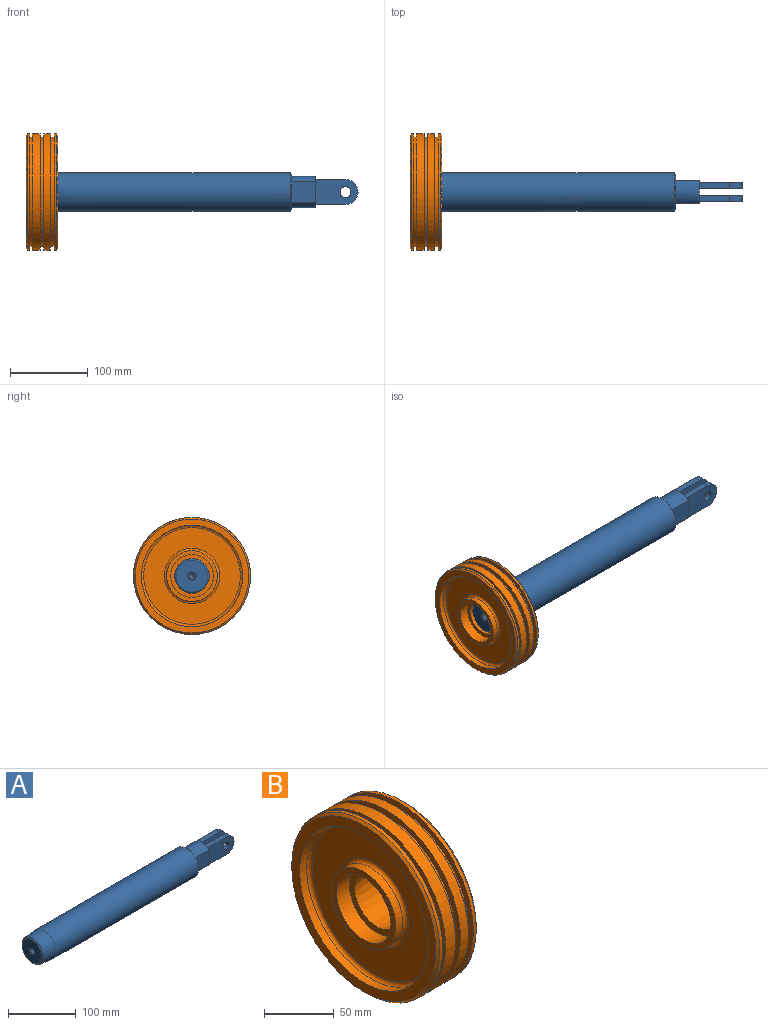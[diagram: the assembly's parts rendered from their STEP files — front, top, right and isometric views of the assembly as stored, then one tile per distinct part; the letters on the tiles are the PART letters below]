
ASSEMBLY  parts=2 mates=1
PART A: 28 faces, bbox 410x50x50 mm
  f0: plane 32x3mm, normal (1,0,0), area 88.3mm2, adj f1,f4,f21,f24
  f1: cylinder r=20mm len=30mm, axis (1,0,0), area 1017.7mm2, adj f0,f2,f3,f5,f23,f24
  f2: plane 40x24mm, normal (1,0,0), area 386.8mm2, adj f1,f4,f11,f12,f16,f17,f19,f22
  f3: plane 32x3mm, normal (1,0,0), area 88.3mm2, adj f1,f4,f15,f23
  f4: cylinder r=20mm len=30mm, axis (1,0,0), area 1017.7mm2, adj f0,f2,f3,f5,f23,f24
  f5: plane 45.58x45.58mm, normal (1,0,0), area 556.4mm2, adj f1,f4,f9,f23,f24
  f6: cylinder r=25mm len=297.79mm, axis (1,0,0), area 46776.8mm2, adj f7,f9
  f7: cone r=22.5mm half-angle=5.7deg, axis (1,0,0), area 3465.5mm2, adj f6,f10
  f8: plane 41.01x41.01mm, normal (-1,0,0), area 1234.3mm2, adj f10,f27
  f9: cone r=22.79mm half-angle=45deg, axis (-1,0,0), area 469.2mm2, adj f5,f6
  f10: cone r=22.7mm half-angle=47.8deg, axis (1,0,0), area 402.6mm2, adj f7,f8
  f11: plane 39x8mm, normal (0,0,1), area 312mm2, adj f2,f14,f15,f16
  f12: plane 39x8mm, normal (0,0,-1), area 312mm2, adj f2,f14,f15,f16
  f13: cylinder r=7mm len=14mm, axis (0,1,0), area 351.9mm2, adj f15,f16
  f14: cylinder r=16mm len=32mm, axis (0,1,0), area 402.1mm2, adj f11,f12,f15,f16
  f15: plane 55x32mm, normal (0,-1,0), area 1496.2mm2, adj f3,f11,f12,f13,f14
  f16: plane 55x32mm, normal (0,1,0), area 1496.2mm2, adj f2,f11,f12,f13,f14
  f17: plane 39x8mm, normal (0,0,1), area 312mm2, adj f2,f18,f21,f22
  f18: cylinder r=16mm len=32mm, axis (0,-1,0), area 402.1mm2, adj f17,f19,f21,f22
  f19: plane 39x8mm, normal (0,0,-1), area 312mm2, adj f2,f18,f21,f22
  f20: cylinder r=7mm len=14mm, axis (0,-1,0), area 351.9mm2, adj f21,f22
  f21: plane 55x32mm, normal (0,1,0), area 1496.2mm2, adj f0,f17,f18,f19,f20
  f22: plane 55x32mm, normal (0,-1,0), area 1496.2mm2, adj f2,f17,f18,f19,f20
  f23: plane 30x26.46mm, normal (0,-1,0), area 793.7mm2, adj f1,f3,f4,f5
  f24: plane 30x26.46mm, normal (0,1,0), area 793.7mm2, adj f0,f1,f4,f5
  f25: cone r=0mm half-angle=59deg, axis (-1,0,0), area 66.2mm2, adj f26
  f26: cylinder r=4.25mm len=24mm, axis (-1,0,0), area 640.9mm2, adj f25,f27
  f27: cone r=4.25mm half-angle=45deg, axis (-1,0,0), area 42.2mm2, adj f8,f26
PART B: 32 faces, bbox 41x150x150 mm
  f0: plane 150x150mm, normal (-1,0,0), area 2277.7mm2, adj f1,f29
  f1: cylinder r=70mm len=140mm, axis (-1,0,0), area 2199.1mm2, adj f0,f2
  f2: plane 150x150mm, normal (1,0,0), area 2277.7mm2, adj f1,f3
  f3: cylinder r=75mm len=150mm, axis (-1,0,0), area 3769.9mm2, adj f2,f4
  f4: plane 150x150mm, normal (-1,0,0), area 2277.7mm2, adj f3,f5
  f5: cylinder r=70mm len=140mm, axis (-1,0,0), area 2199.1mm2, adj f4,f6
  f6: plane 150x150mm, normal (1,0,0), area 2277.7mm2, adj f5,f7
  f7: cylinder r=75mm len=150mm, axis (-1,0,0), area 4712.4mm2, adj f6,f8
  f8: plane 150x150mm, normal (-1,0,0), area 2277.7mm2, adj f7,f9
  f9: cylinder r=70mm len=140mm, axis (-1,0,0), area 1319.5mm2, adj f8,f10
  f10: plane 150x150mm, normal (1,0,0), area 2277.7mm2, adj f9,f11
  f11: cylinder r=75mm len=150mm, axis (-1,0,0), area 1413.7mm2, adj f10,f30
  f12: plane 146x146mm, normal (-1,0,0), area 3468.3mm2, adj f13,f30
  f13: cylinder r=65mm len=130mm, axis (-1,0,0), area 2858.8mm2, adj f12,f14
  f14: torus R=62mm, axis (-1,0,0), area 1892.3mm2, adj f13,f15
  f15: plane 124x124mm, normal (-1,0,0), area 8117.1mm2, adj f14,f16
  f16: torus R=35.5mm, axis (-1,0,0), area 994.6mm2, adj f15,f17
  f17: cylinder r=32.5mm len=65mm, axis (-1,0,0), area 1429.4mm2, adj f16,f18
  f18: plane 65x65mm, normal (-1,0,0), area 942.5mm2, adj f17,f19
  f19: cylinder r=27.5mm len=55mm, axis (-1,0,0), area 2246.2mm2, adj f18,f20
  f20: plane 55x55mm, normal (-1,0,0), area 826.8mm2, adj f19,f21
  f21: cone r=22.21mm half-angle=5.7deg, axis (1,0,0), area 4173mm2, adj f20,f22
  f22: plane 65x65mm, normal (1,0,0), area 1354.8mm2, adj f21,f23
  f23: cylinder r=32.5mm len=65mm, axis (-1,0,0), area 1429.4mm2, adj f22,f24
  f24: torus R=35.5mm, axis (-1,0,0), area 994.6mm2, adj f23,f25
  f25: plane 124x124mm, normal (1,0,0), area 8117.1mm2, adj f24,f26
  f26: torus R=62mm, axis (-1,0,0), area 1892.3mm2, adj f25,f27
  f27: cylinder r=65mm len=130mm, axis (-1,0,0), area 2858.8mm2, adj f26,f28
  f28: plane 146x146mm, normal (1,0,0), area 3468.3mm2, adj f27,f31
  f29: cylinder r=75mm len=150mm, axis (-1,0,0), area 1413.7mm2, adj f0,f31
  f30: cone r=73mm half-angle=45deg, axis (1,0,0), area 1315.1mm2, adj f11,f12
  f31: cone r=75mm half-angle=45deg, axis (-1,0,0), area 1315.1mm2, adj f28,f29
PLACE A at identity fixed
PLACE B t=(-341,0,0)mm
MATE fastened B.f1 <-> A.f1  axis (1,0,0) through (-300,0,0)mm
